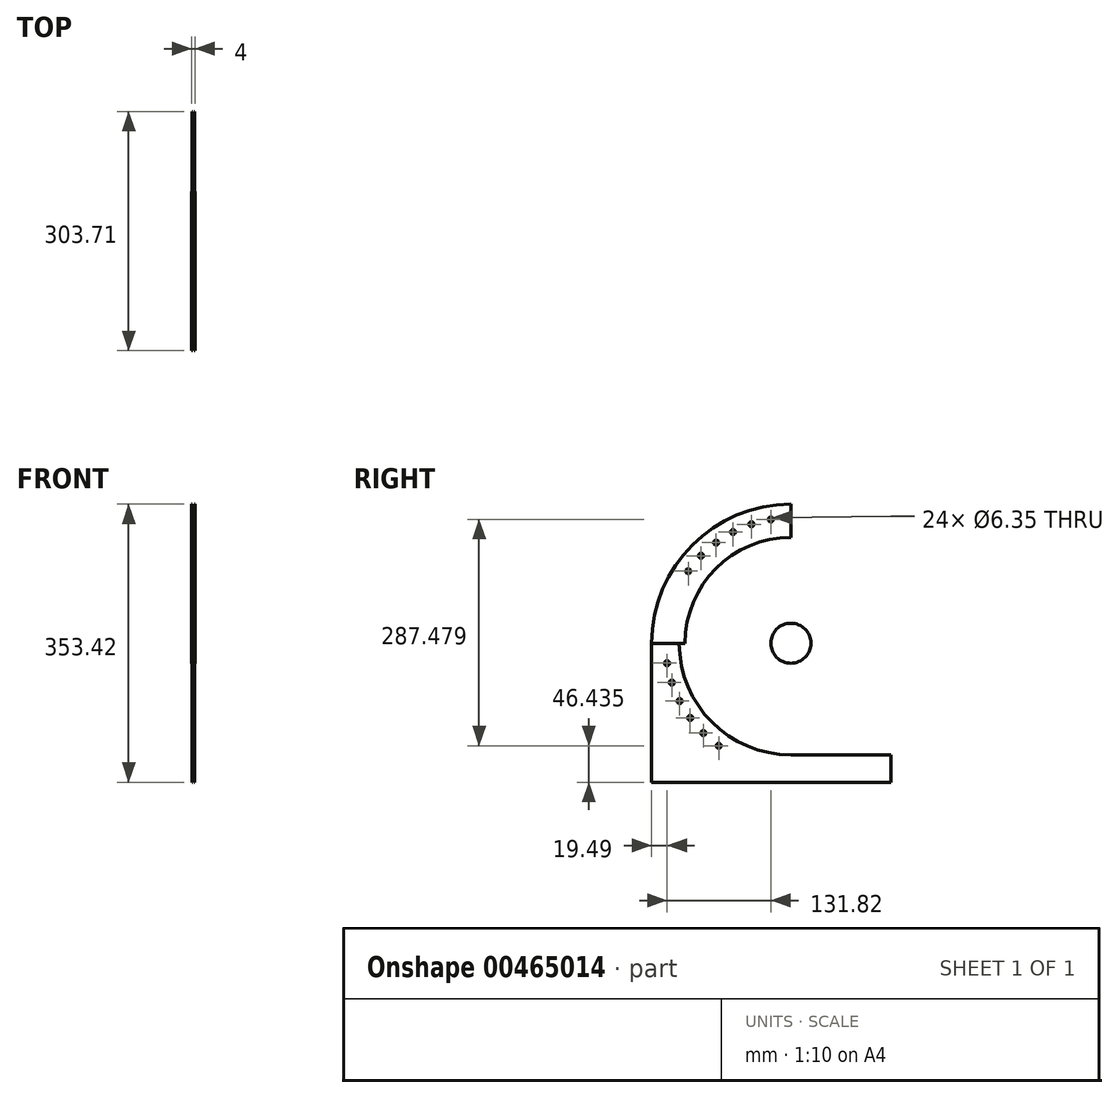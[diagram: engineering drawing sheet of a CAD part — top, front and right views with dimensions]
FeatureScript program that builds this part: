
annotation { "Feature Type Name" : "Feature", "Feature Type Description" : "" }
export const myFeature = defineFeature(function(context is Context, id is Id, definition is map)
    precondition{}
    {
        {
            assignVariable(context, id + "F0", {"name" : "trw", "anyValue" : .5});
        }
        {
            assignVariable(context, id + "F1", {"name" : "trsp", "anyValue" : 2});
        }
        {
            assignVariable(context, id + "F2", {"name" : "shwhw", "anyValue" : 1});
        }
        {
            var Q0;
            Q0=qCreatedBy(makeId("Right.planeOp"),FACE);
            cPlane(context, id + "F3", {"entities" : qUnion([Q0]), "cplaneType" : CPlaneType.OFFSET, "offset" : (getVariable(context, 'trsp') / 2) * mm, "width" : 152.4 * mm, "height" : 152.4 * mm});
        }
        {
            var Q0;
            Q0=qCreatedBy(id+"F3.planeOp",FACE);
            var sketch = newSketch(context, id + "F4", { "sketchPlane" : qUnion([Q0])});
            skLineSegment(sketch, "E0.bottom", {"start": v(0, 0) * mm, "end": v(127, 0) * mm});
            skLineSegment(sketch, "E0.top", {"start": v(0, 34.93) * mm, "end": v(127, 34.93) * mm});
            skLineSegment(sketch, "E0.left", {"start": v(0, 0) * mm, "end": v(0, 34.93) * mm});
            skLineSegment(sketch, "E0.right", {"start": v(127, 0) * mm, "end": v(127, 34.92) * mm});
            skCircle(sketch, "E1", {"center": v(0, 176.7) * mm, "radius": 25.4 * mm});
            skArc(sketch, "E2", {"start": v(-141.78, 176.7) * mm, "mid": v(-100.26, 76.45) * mm, "end": v(0, 34.92) * mm});
            skArc(sketch, "E3", {"start": v(-176.7, 176.7) * mm, "mid": v(-124.95, 51.76) * mm, "end": v(0, 0) * mm});
            skLineSegment(sketch, "E4", {"start": v(-141.78, 176.7) * mm, "end": v(-176.7, 176.7) * mm});
            skLineSegment(sketch, "E5", {"start": v(0, 0) * mm, "end": v(-176.7, 0) * mm});
            skLineSegment(sketch, "E6", {"start": v(-176.7, 0) * mm, "end": v(-176.7, 176.7) * mm});
            skPoint(sketch, "E7", {"position": v(-159.25, 176.7) * mm});
            skCircle(sketch, "E8", {"center": v(0, 176.7) * mm, "radius": 159.25 * mm, "construction": true});
            skCircle(sketch, "E9", {"center": v(-157.22, 151.39) * mm, "radius": 3.18 * mm});
            skCircle(sketch, "E10.1.0", {"center": v(-151.2, 126.71) * mm, "radius": 3.18 * mm});
            skCircle(sketch, "E10.2.0", {"center": v(-141.32, 103.31) * mm, "radius": 3.18 * mm});
            skCircle(sketch, "E10.3.0", {"center": v(-127.85, 81.77) * mm, "radius": 3.17 * mm});
            skCircle(sketch, "E10.4.0", {"center": v(-111.13, 62.65) * mm, "radius": 3.18 * mm});
            skCircle(sketch, "E10.5.0", {"center": v(-91.59, 46.44) * mm, "radius": 3.18 * mm});
            skLineSegment(sketch, "E10.anchor1", {"start": v(0, 176.7) * mm, "end": v(-157.22, 151.39) * mm, "construction": true});
            skLineSegment(sketch, "E10.anchor2", {"start": v(0, 176.7) * mm, "end": v(-91.59, 46.44) * mm, "construction": true});
            skSolve(sketch);
        }
        {
            var Q0;
            Q0=makeQuery(id+"F4.imprint","IMPRINT",FACE,{"disambiguationData":[TD([[makeQuery(id+"F4.imprint","IMPRINT",EDGE,{"derivedFrom":sQuery(id+"F4.wireOp",EDGE,"E1")}),1.0]])]});
            extrude(context, id + "F5", {"entities" : qUnion([Q0]), "depth" : (getVariable(context, 'shwhw')) * mm});
        }
        {
            var Q0;
            Q0=makeQuery(id+"F4.imprint","IMPRINT",FACE,{"disambiguationData":[TD([[makeQuery(id+"F4.imprint","IMPRINT",EDGE,{"derivedFrom":sQuery(id+"F4.wireOp",EDGE,"E0.left")}),1.0]])]});
            var Q1;
            Q1=makeQuery(id+"F4.imprint","IMPRINT",FACE,{"disambiguationData":[TD([[makeQuery(id+"F4.imprint","IMPRINT",EDGE,{"derivedFrom":sQuery(id+"F4.wireOp",EDGE,"E0.bottom")}),1.0]])]});
            extrude(context, id + "F6", {"entities" : qUnion([Q0, Q1]), "depth" : (getVariable(context, 'trw')) * mm});
        }
        {
            var Q0;
            Q0=makeQuery(id+"F4.imprint","IMPRINT",FACE,{"disambiguationData":[TD([[makeQuery(id+"F4.imprint","IMPRINT",EDGE,{"derivedFrom":sQuery(id+"F4.wireOp",EDGE,"E3")}),-1.0]])]});
            extrude(context, id + "F7", {"entities" : qUnion([Q0]), "operationType" : NewBodyOperationType.ADD, "depth" : (getVariable(context, 'trw')) * mm});
        }
        {
            var Q0;
            Q0=qCreatedBy(makeId("Right.planeOp"),FACE);
            cPlane(context, id + "F8", {"entities" : qUnion([Q0]), "cplaneType" : CPlaneType.OFFSET, "offset" : (getVariable(context, 'trsp') / 2 + getVariable(context, 'trw')) * mm, "width" : 152.4 * mm, "height" : 152.4 * mm});
        }
        {
            var Q0;
            Q0=qCreatedBy(id+"F8.planeOp",FACE);
            var sketch = newSketch(context, id + "F9", { "sketchPlane" : qUnion([Q0])});
            skCircle(sketch, "E11.0.0", {"center": v(0, 176.7) * mm, "radius": 25.4 * mm});
            skArc(sketch, "E12", {"start": v(0, 311.1) * mm, "mid": v(-95.03, 271.74) * mm, "end": v(-134.4, 176.7) * mm});
            skArc(sketch, "E13", {"start": v(0, 353.42) * mm, "mid": v(-124.95, 301.66) * mm, "end": v(-176.7, 176.7) * mm});
            skLineSegment(sketch, "E14", {"start": v(0, 353.42) * mm, "end": v(0, 311.1) * mm});
            skLineSegment(sketch, "E15", {"start": v(-134.4, 176.7) * mm, "end": v(-220.4, 176.7) * mm});
            skCircle(sketch, "E16", {"center": v(-25.4, 333.91) * mm, "radius": 3.18 * mm});
            skCircle(sketch, "E17.1.0", {"center": v(-50.07, 327.88) * mm, "radius": 3.18 * mm});
            skCircle(sketch, "E17.2.0", {"center": v(-73.47, 318) * mm, "radius": 3.18 * mm});
            skCircle(sketch, "E17.3.0", {"center": v(-95, 304.51) * mm, "radius": 3.17 * mm});
            skCircle(sketch, "E17.4.0", {"center": v(-114.11, 287.78) * mm, "radius": 3.18 * mm});
            skCircle(sketch, "E17.5.0", {"center": v(-130.32, 268.23) * mm, "radius": 3.18 * mm});
            skLineSegment(sketch, "E17.anchor1", {"start": v(0, 176.7) * mm, "end": v(-25.4, 333.91) * mm, "construction": true});
            skLineSegment(sketch, "E17.anchor2", {"start": v(0, 176.7) * mm, "end": v(-130.32, 268.23) * mm, "construction": true});
            skSolve(sketch);
        }
        {
            var Q0;
            {var subQ0=sQuery(id+"F9.wireOp",EDGE,"E12");Q0=makeQuery(id+"F9.imprint","IMPRINT",FACE,{"disambiguationData":[TD([[makeQuery(id+"F9.imprint","IMPRINT",EDGE,{"derivedFrom":subQ0}),-1.0]])]});}
            extrude(context, id + "F10", {"entities" : qUnion([Q0]), "depth" : (getVariable(context, 'trw')) * mm});
        }
        {
            var Q0;
            Q0=makeQuery(id+"F10.opExtrude","SWEPT_BODY",BODY,{"disambiguationData":[OSD([sQuery(id+"F9.wireOp",EDGE,"E12"),sQuery(id+"F9.wireOp",EDGE,"E13"),sQuery(id+"F9.wireOp",EDGE,"E14"),sQuery(id+"F9.wireOp",EDGE,"E15")])]});
            var Q1;
            Q1=makeQuery(id+"F5.opExtrude","SWEPT_BODY",BODY,{"disambiguationData":[OSD([sQuery(id+"F4.wireOp",EDGE,"E1")])]});
            var Q2;
            Q2=makeQuery(id+"F6.opExtrude","SWEPT_BODY",BODY,{"disambiguationData":[OSD([sQuery(id+"F4.wireOp",EDGE,"E0.bottom"),sQuery(id+"F4.wireOp",EDGE,"E0.top"),sQuery(id+"F4.wireOp",EDGE,"E0.right"),sQuery(id+"F4.wireOp",EDGE,"E2"),sQuery(id+"F4.wireOp",EDGE,"E3"),sQuery(id+"F4.wireOp",EDGE,"E4")])]});
            var Q3;
            Q3=qCreatedBy(makeId("Right.planeOp"),FACE);
            mirror(context, id + "F11", {"entities" : qUnion([Q0, Q1, Q2]), "mirrorPlane" : qUnion([Q3])});
        }
    });
